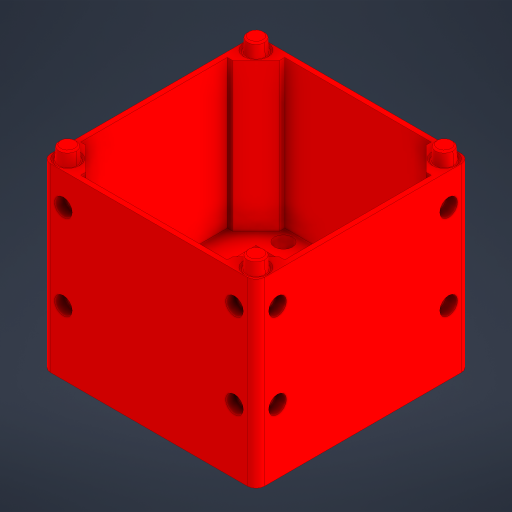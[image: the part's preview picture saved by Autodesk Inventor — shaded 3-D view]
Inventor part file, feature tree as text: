
AUTODESK INVENTOR PART (.ipt)
format: ipt  version: 2023.4 (Build 274418000, 418)  size: 365,568 bytes
history: native  units: mm
features: extrude x8, chamfer x7, projected_geometry x2, pattern_linear x1, pattern_circular x1, fillet x1
ambient origin geometry x8: Origin, YZ Plane, XZ Plane, XY Plane, X Axis, Y Axis, Z Axis, Center Point
bodies: Solid1 (feature_tree)
feature tree (20):
  extrude  "Extrusion1"  Depth=49.8mm
  extrude  "Extrusion2"  Depth=49.8mm
  extrude  "Extrusion3"  Depth=8.0mm
  extrude  "Extrusion4"  Depth=10.5mm
  chamfer  "Chamfer1"  Distance=10.5mm
  chamfer  "Chamfer2"  Distance=4.1mm
  chamfer  "Chamfer3"  Distance=4.15mm
  chamfer  "Chamfer4"  Distance=3.0mm
  chamfer  "Chamfer5"  Distance=3.0mm
  chamfer  "Chamfer6"  Distance=4.2625mm
  extrude  "Extrusion5"  Depth=0.675mm
  extrude  "Extrusion6"  Depth=7.85mm
  pattern_linear  "Rectangular Pattern1"  Spacing1=7.85mm  [1 undecoded]
  pattern_circular  "Circular Pattern1"  [2 undecoded]
  extrude  "Extrusion7"  Depth=5.5mm
  fillet  "Fillet1"  Radius=40.0mm
  chamfer  "Chamfer7"  Distance=7.7mm
  extrude  "Extrusion8"  Depth=34.4mm TaperAngle=0.0deg
  projected_geometry  "Projected Loop1"
  projected_geometry  "Projected Loop2"
note: 3 required parameter values undecoded (feature->parameter linkage not recoverable at this tier; creation-order binding heuristic only, values carry confidence <= 0.55)
